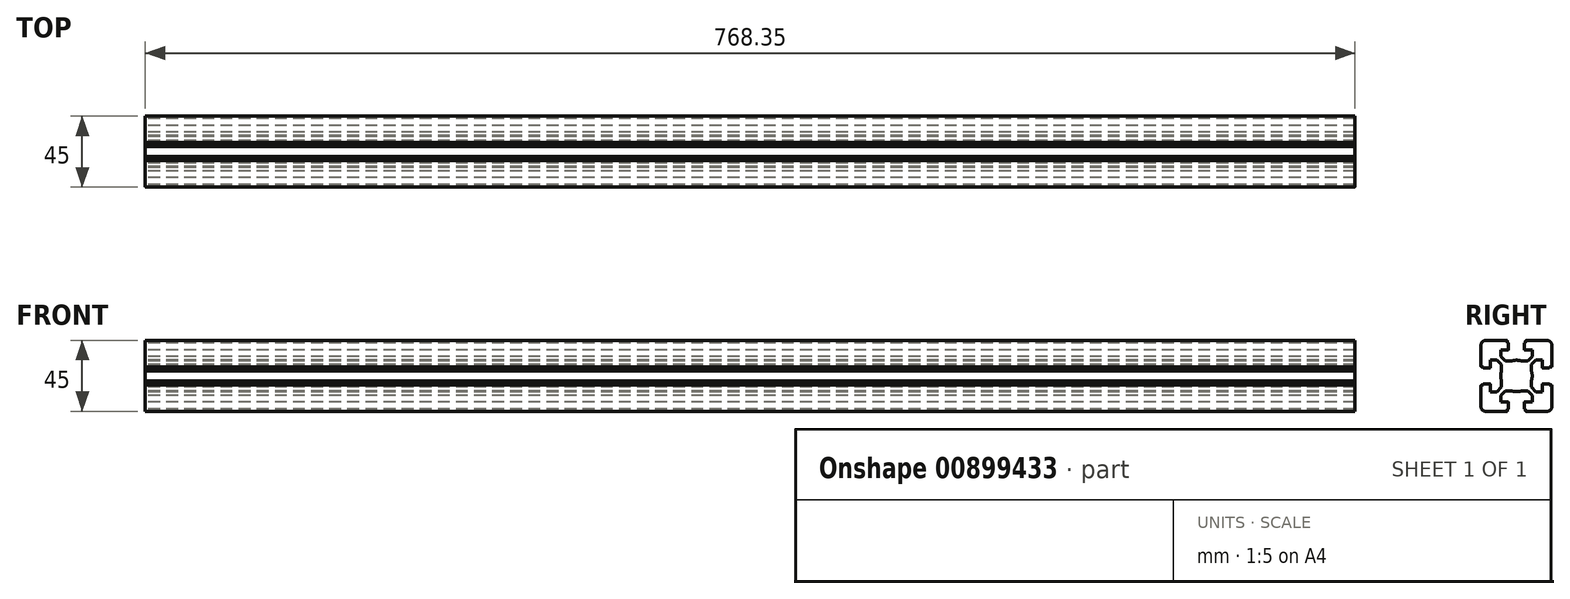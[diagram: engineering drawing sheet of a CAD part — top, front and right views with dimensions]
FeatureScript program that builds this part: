
annotation { "Feature Type Name" : "Feature", "Feature Type Description" : "" }
export const myFeature = defineFeature(function(context is Context, id is Id, definition is map)
    precondition{}
    {
        {
            var Q0;
            Q0=qCreatedBy(makeId("Right.planeOp"),FACE);
            var sketch = newSketch(context, id + "F0", { "sketchPlane" : qUnion([Q0])});
            skLineSegment(sketch, "E0", {"start": v(-20.09, -10.29) * mm, "end": v(-21.29, -10.29) * mm});
            skArc(sketch, "E1", {"start": v(-21.29, -10.29) * mm, "mid": v(-21.5, -10.38) * mm, "end": v(-21.59, -10.59) * mm});
            skLineSegment(sketch, "E2", {"start": v(-21.59, -10.59) * mm, "end": v(-21.59, -23.99) * mm});
            skArc(sketch, "E3", {"start": v(-21.59, -23.99) * mm, "mid": v(-20.7, -26.11) * mm, "end": v(-18.59, -26.99) * mm});
            skLineSegment(sketch, "E4", {"start": v(-18.59, -26.99) * mm, "end": v(-5.19, -26.99) * mm});
            skArc(sketch, "E5", {"start": v(-5.19, -26.99) * mm, "mid": v(-4.98, -26.9) * mm, "end": v(-4.89, -26.69) * mm});
            skLineSegment(sketch, "E6", {"start": v(-4.89, -26.69) * mm, "end": v(-4.89, -25.49) * mm});
            skLineSegment(sketch, "E7", {"start": v(-4.89, -25.49) * mm, "end": v(-4.39, -25.49) * mm});
            skArc(sketch, "E8", {"start": v(-4.39, -25.49) * mm, "mid": v(-4.18, -25.4) * mm, "end": v(-4.09, -25.19) * mm});
            skLineSegment(sketch, "E9", {"start": v(-4.09, -25.19) * mm, "end": v(-4.09, -21.29) * mm});
            skArc(sketch, "E10", {"start": v(-4.09, -21.29) * mm, "mid": v(-4.18, -21.08) * mm, "end": v(-4.39, -20.99) * mm});
            skLineSegment(sketch, "E11", {"start": v(-4.39, -20.99) * mm, "end": v(-9.14, -20.99) * mm});
            skLineSegment(sketch, "E12", {"start": v(-9.14, -20.99) * mm, "end": v(-9.14, -16.88) * mm});
            skLineSegment(sketch, "E13", {"start": v(-9.14, -16.88) * mm, "end": v(-6.25, -13.99) * mm});
            skLineSegment(sketch, "E14", {"start": v(-6.25, -13.99) * mm, "end": v(-2.21, -13.99) * mm});
            skArc(sketch, "E15", {"start": v(-2.21, -13.99) * mm, "mid": v(0.91, -14.49) * mm, "end": v(4.03, -13.99) * mm});
            skLineSegment(sketch, "E16", {"start": v(-20.09, -10.29) * mm, "end": v(-20.09, -9.79) * mm});
            skArc(sketch, "E17", {"start": v(-20.09, -9.79) * mm, "mid": v(-20, -9.58) * mm, "end": v(-19.79, -9.49) * mm});
            skLineSegment(sketch, "E18", {"start": v(-19.79, -9.49) * mm, "end": v(-15.89, -9.49) * mm});
            skArc(sketch, "E19", {"start": v(-15.89, -9.49) * mm, "mid": v(-15.68, -9.58) * mm, "end": v(-15.59, -9.79) * mm});
            skLineSegment(sketch, "E20", {"start": v(-15.59, -9.79) * mm, "end": v(-15.59, -14.54) * mm});
            skLineSegment(sketch, "E21", {"start": v(-15.59, -14.54) * mm, "end": v(-11.48, -14.54) * mm});
            skLineSegment(sketch, "E22", {"start": v(-11.48, -14.54) * mm, "end": v(-8.59, -11.65) * mm});
            skLineSegment(sketch, "E23", {"start": v(-8.59, -11.65) * mm, "end": v(-8.59, -7.61) * mm});
            skLineSegment(sketch, "E24", {"start": v(29.82, -4.49) * mm, "end": v(-31.05, -4.49) * mm});
            skLineSegment(sketch, "E25.MirrorCS", {"start": v(6.71, -25.49) * mm, "end": v(6.21, -25.49) * mm});
            skArc(sketch, "E26.MirrorCS", {"start": v(7.01, -26.99) * mm, "mid": v(6.8, -26.9) * mm, "end": v(6.71, -26.69) * mm});
            skLineSegment(sketch, "E27.MirrorCS", {"start": v(10.41, -11.65) * mm, "end": v(10.41, -7.61) * mm});
            skArc(sketch, "E28.MirrorCS", {"start": v(6.21, -25.49) * mm, "mid": v(6, -25.4) * mm, "end": v(5.91, -25.19) * mm});
            skLineSegment(sketch, "E29.MirrorCS", {"start": v(6.71, -26.69) * mm, "end": v(6.71, -25.49) * mm});
            skArc(sketch, "E30.MirrorCS", {"start": v(5.91, -21.29) * mm, "mid": v(6, -21.08) * mm, "end": v(6.21, -20.99) * mm});
            skLineSegment(sketch, "E31.MirrorCS", {"start": v(10.96, -16.88) * mm, "end": v(8.07, -13.99) * mm});
            skLineSegment(sketch, "E32.MirrorCS", {"start": v(13.3, -14.54) * mm, "end": v(10.41, -11.65) * mm});
            skLineSegment(sketch, "E33.MirrorCS", {"start": v(17.41, -14.54) * mm, "end": v(13.3, -14.54) * mm});
            skLineSegment(sketch, "E34.MirrorCS", {"start": v(17.41, -9.79) * mm, "end": v(17.41, -14.54) * mm});
            skLineSegment(sketch, "E35.MirrorCS", {"start": v(6.21, -20.99) * mm, "end": v(10.96, -20.99) * mm});
            skLineSegment(sketch, "E36.MirrorCS", {"start": v(8.07, -13.99) * mm, "end": v(4.03, -13.99) * mm});
            skArc(sketch, "E37.MirrorCS", {"start": v(4.03, -13.99) * mm, "mid": v(0.91, -14.49) * mm, "end": v(-2.21, -13.99) * mm});
            skLineSegment(sketch, "E38.MirrorCS", {"start": v(10.96, -20.99) * mm, "end": v(10.96, -16.88) * mm});
            skLineSegment(sketch, "E39.MirrorCS", {"start": v(5.91, -25.19) * mm, "end": v(5.91, -21.29) * mm});
            skArc(sketch, "E40.MirrorCS", {"start": v(23.41, -23.99) * mm, "mid": v(22.53, -26.11) * mm, "end": v(20.41, -26.99) * mm});
            skLineSegment(sketch, "E41.MirrorCS", {"start": v(20.41, -26.99) * mm, "end": v(7.01, -26.99) * mm});
            skLineSegment(sketch, "E42.MirrorCS", {"start": v(23.41, -10.59) * mm, "end": v(23.41, -23.99) * mm});
            skArc(sketch, "E43.MirrorCS", {"start": v(17.71, -9.49) * mm, "mid": v(17.5, -9.58) * mm, "end": v(17.41, -9.79) * mm});
            skArc(sketch, "E44.MirrorCS", {"start": v(23.11, -10.29) * mm, "mid": v(23.32, -10.38) * mm, "end": v(23.41, -10.59) * mm});
            skLineSegment(sketch, "E45.MirrorCS", {"start": v(21.91, -10.29) * mm, "end": v(21.91, -9.79) * mm});
            skLineSegment(sketch, "E46.MirrorCS", {"start": v(21.91, -10.29) * mm, "end": v(23.11, -10.29) * mm});
            skArc(sketch, "E47.MirrorCS", {"start": v(21.91, -9.79) * mm, "mid": v(21.82, -9.58) * mm, "end": v(21.61, -9.49) * mm});
            skLineSegment(sketch, "E48.MirrorCS", {"start": v(21.61, -9.49) * mm, "end": v(17.71, -9.49) * mm});
            skLineSegment(sketch, "E49.MirrorCS", {"start": v(6.71, 16.51) * mm, "end": v(6.21, 16.51) * mm});
            skArc(sketch, "E50.MirrorCS", {"start": v(-4.39, 16.51) * mm, "mid": v(-4.18, 16.42) * mm, "end": v(-4.09, 16.21) * mm});
            skLineSegment(sketch, "E51.MirrorCS", {"start": v(-4.89, 16.51) * mm, "end": v(-4.39, 16.51) * mm});
            skArc(sketch, "E52.MirrorCS", {"start": v(5.91, 12.31) * mm, "mid": v(6, 12.1) * mm, "end": v(6.21, 12.01) * mm});
            skLineSegment(sketch, "E53.MirrorCS", {"start": v(6.71, 17.71) * mm, "end": v(6.71, 16.51) * mm});
            skLineSegment(sketch, "E54.MirrorCS", {"start": v(-4.89, 17.71) * mm, "end": v(-4.89, 16.51) * mm});
            skArc(sketch, "E55.MirrorCS", {"start": v(-5.19, 18.01) * mm, "mid": v(-4.98, 17.92) * mm, "end": v(-4.89, 17.71) * mm});
            skArc(sketch, "E56.MirrorCS", {"start": v(-4.09, 12.31) * mm, "mid": v(-4.18, 12.1) * mm, "end": v(-4.39, 12.01) * mm});
            skArc(sketch, "E57.MirrorCS", {"start": v(7.01, 18.01) * mm, "mid": v(6.8, 17.92) * mm, "end": v(6.71, 17.71) * mm});
            skArc(sketch, "E58.MirrorCS", {"start": v(6.21, 16.51) * mm, "mid": v(6, 16.42) * mm, "end": v(5.91, 16.21) * mm});
            skArc(sketch, "E59.MirrorCS", {"start": v(23.11, 1.31) * mm, "mid": v(23.32, 1.4) * mm, "end": v(23.41, 1.61) * mm});
            skLineSegment(sketch, "E60.MirrorCS", {"start": v(21.91, 1.31) * mm, "end": v(21.91, 0.81) * mm});
            skArc(sketch, "E61.MirrorCS", {"start": v(-15.89, 0.51) * mm, "mid": v(-15.68, 0.6) * mm, "end": v(-15.59, 0.81) * mm});
            skArc(sketch, "E62.MirrorCS", {"start": v(-21.29, 1.31) * mm, "mid": v(-21.5, 1.4) * mm, "end": v(-21.59, 1.61) * mm});
            skArc(sketch, "E63.MirrorCS", {"start": v(17.71, 0.51) * mm, "mid": v(17.5, 0.6) * mm, "end": v(17.41, 0.81) * mm});
            skArc(sketch, "E64.MirrorCS", {"start": v(21.91, 0.81) * mm, "mid": v(21.82, 0.6) * mm, "end": v(21.61, 0.51) * mm});
            skLineSegment(sketch, "E65.MirrorCS", {"start": v(21.91, 1.31) * mm, "end": v(23.11, 1.31) * mm});
            skArc(sketch, "E66.MirrorCS", {"start": v(14.31, 5.31) * mm, "mid": v(14.1, 5.4) * mm, "end": v(14.01, 5.61) * mm});
            skArc(sketch, "E67.MirrorCS", {"start": v(-20.09, 0.81) * mm, "mid": v(-20, 0.6) * mm, "end": v(-19.79, 0.51) * mm});
            skLineSegment(sketch, "E68.MirrorCS", {"start": v(-20.09, 1.31) * mm, "end": v(-21.29, 1.31) * mm});
            skLineSegment(sketch, "E69.MirrorCS", {"start": v(-20.09, 1.31) * mm, "end": v(-20.09, 0.81) * mm});
            skLineSegment(sketch, "E70.MirrorCS", {"start": v(8.07, 5.01) * mm, "end": v(4.03, 5.01) * mm});
            skLineSegment(sketch, "E71.MirrorCS", {"start": v(-4.09, 16.21) * mm, "end": v(-4.09, 12.31) * mm});
            skLineSegment(sketch, "E72.MirrorCS", {"start": v(-9.14, 12.01) * mm, "end": v(-9.14, 7.9) * mm});
            skLineSegment(sketch, "E73.MirrorCS", {"start": v(-15.59, 5.56) * mm, "end": v(-11.48, 5.56) * mm});
            skLineSegment(sketch, "E74.MirrorCS", {"start": v(-4.39, 12.01) * mm, "end": v(-9.14, 12.01) * mm});
            skLineSegment(sketch, "E75.MirrorCS", {"start": v(-9.14, 7.9) * mm, "end": v(-6.25, 5.01) * mm});
            skLineSegment(sketch, "E76.MirrorCS", {"start": v(10.96, 12.01) * mm, "end": v(10.96, 7.9) * mm});
            skArc(sketch, "E77.MirrorCS", {"start": v(-21.59, 15.01) * mm, "mid": v(-20.7, 17.13) * mm, "end": v(-18.59, 18.01) * mm});
            skLineSegment(sketch, "E78.MirrorCS", {"start": v(23.41, 1.61) * mm, "end": v(23.41, 15.01) * mm});
            skLineSegment(sketch, "E79.MirrorCS", {"start": v(13.3, 5.56) * mm, "end": v(10.41, 2.67) * mm});
            skLineSegment(sketch, "E80.MirrorCS", {"start": v(-8.59, 2.67) * mm, "end": v(-8.59, -1.37) * mm});
            skLineSegment(sketch, "E81.MirrorCS", {"start": v(-15.59, 0.81) * mm, "end": v(-15.59, 5.56) * mm});
            skLineSegment(sketch, "E82.MirrorCS", {"start": v(10.41, 2.67) * mm, "end": v(10.41, -1.37) * mm});
            skLineSegment(sketch, "E83.MirrorCS", {"start": v(-18.59, 18.01) * mm, "end": v(-5.19, 18.01) * mm});
            skLineSegment(sketch, "E84.MirrorCS", {"start": v(10.96, 7.9) * mm, "end": v(8.07, 5.01) * mm});
            skLineSegment(sketch, "E85.MirrorCS", {"start": v(17.41, 5.56) * mm, "end": v(13.3, 5.56) * mm});
            skArc(sketch, "E86.MirrorCS", {"start": v(23.41, 15.01) * mm, "mid": v(22.53, 17.13) * mm, "end": v(20.41, 18.01) * mm});
            skLineSegment(sketch, "E87.MirrorCS", {"start": v(5.91, 16.21) * mm, "end": v(5.91, 12.31) * mm});
            skLineSegment(sketch, "E88.MirrorCS", {"start": v(17.41, 0.81) * mm, "end": v(17.41, 5.56) * mm});
            skLineSegment(sketch, "E89.MirrorCS", {"start": v(-11.48, 5.56) * mm, "end": v(-8.59, 2.67) * mm});
            skLineSegment(sketch, "E90.MirrorCS", {"start": v(-6.25, 5.01) * mm, "end": v(-2.21, 5.01) * mm});
            skLineSegment(sketch, "E91.MirrorCS", {"start": v(-21.59, 1.61) * mm, "end": v(-21.59, 15.01) * mm});
            skArc(sketch, "E92.MirrorCS", {"start": v(4.03, 5.01) * mm, "mid": v(0.91, 5.51) * mm, "end": v(-2.21, 5.01) * mm});
            skLineSegment(sketch, "E93.MirrorCS", {"start": v(6.21, 12.01) * mm, "end": v(10.96, 12.01) * mm});
            skArc(sketch, "E94.MirrorCS", {"start": v(-2.21, 5.01) * mm, "mid": v(0.91, 5.51) * mm, "end": v(4.03, 5.01) * mm});
            skLineSegment(sketch, "E95.MirrorCS", {"start": v(20.41, 18.01) * mm, "end": v(7.01, 18.01) * mm});
            skLineSegment(sketch, "E96.MirrorCS", {"start": v(-19.79, 0.51) * mm, "end": v(-15.89, 0.51) * mm});
            skLineSegment(sketch, "E97.MirrorCS", {"start": v(21.61, 0.51) * mm, "end": v(17.71, 0.51) * mm});
            skLineSegment(sketch, "E98.MirrorCS", {"start": v(0.91, -27.65) * mm, "end": v(0.91, 19.82) * mm});
            skArc(sketch, "E99", {"start": v(-8.59, -1.37) * mm, "mid": v(-9.09, -4.49) * mm, "end": v(-8.59, -7.61) * mm});
            skArc(sketch, "E100", {"start": v(10.41, -7.61) * mm, "mid": v(10.91, -4.49) * mm, "end": v(10.41, -1.37) * mm});
            skSolve(sketch);
        }
        {
            var Q0;
            Q0=qSketchRegion(id+"F0",true);
            extrude(context, id + "F1", {"entities" : qUnion([Q0]), "depth" : 768.35 * mm, "offsetDistance" : 25.4 * mm});
        }
    });
